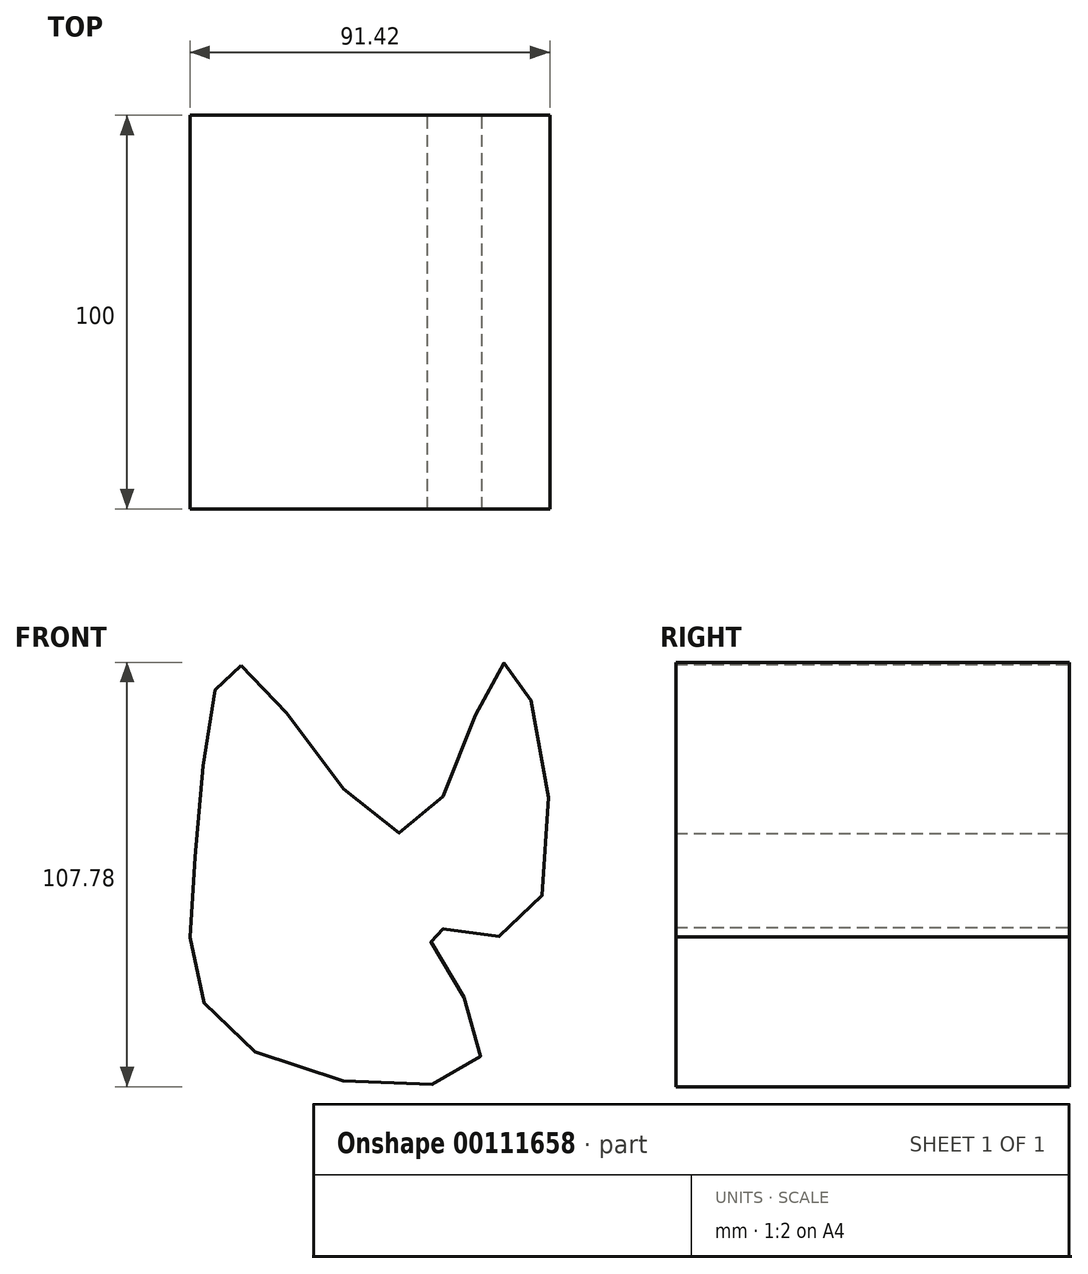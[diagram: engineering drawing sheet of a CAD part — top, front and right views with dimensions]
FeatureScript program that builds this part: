
annotation { "Feature Type Name" : "Feature", "Feature Type Description" : "" }
export const myFeature = defineFeature(function(context is Context, id is Id, definition is map)
    precondition{}
    {
        {
            var Q0;
            Q0=qCreatedBy(makeId("Front.planeOp"),FACE);
            var sketch = newSketch(context, id + "F0", { "sketchPlane" : qUnion([Q0])});
            skFitSpline(sketch, "E0", {"points": [v(-51.39, 49.8) * mm, v(-8.65, 7.3) * mm, v(16.2, 50.54) * mm, v(20.92, -16.3) * mm, v(-3.93, -17.3) * mm, v(9.49, -49.35) * mm, v(-51.64, -46.12) * mm, v(-62.57, 6.56) * mm, v(-51.39, 49.8) * mm]});
            skSolve(sketch);
        }
        {
            var Q0;
            Q0 = qSketchRegion(id + "F0", true);
            extrude(context, id + "F1", {"entities" : qUnion([Q0]), "depth" : 100 * mm});
        }
    });
